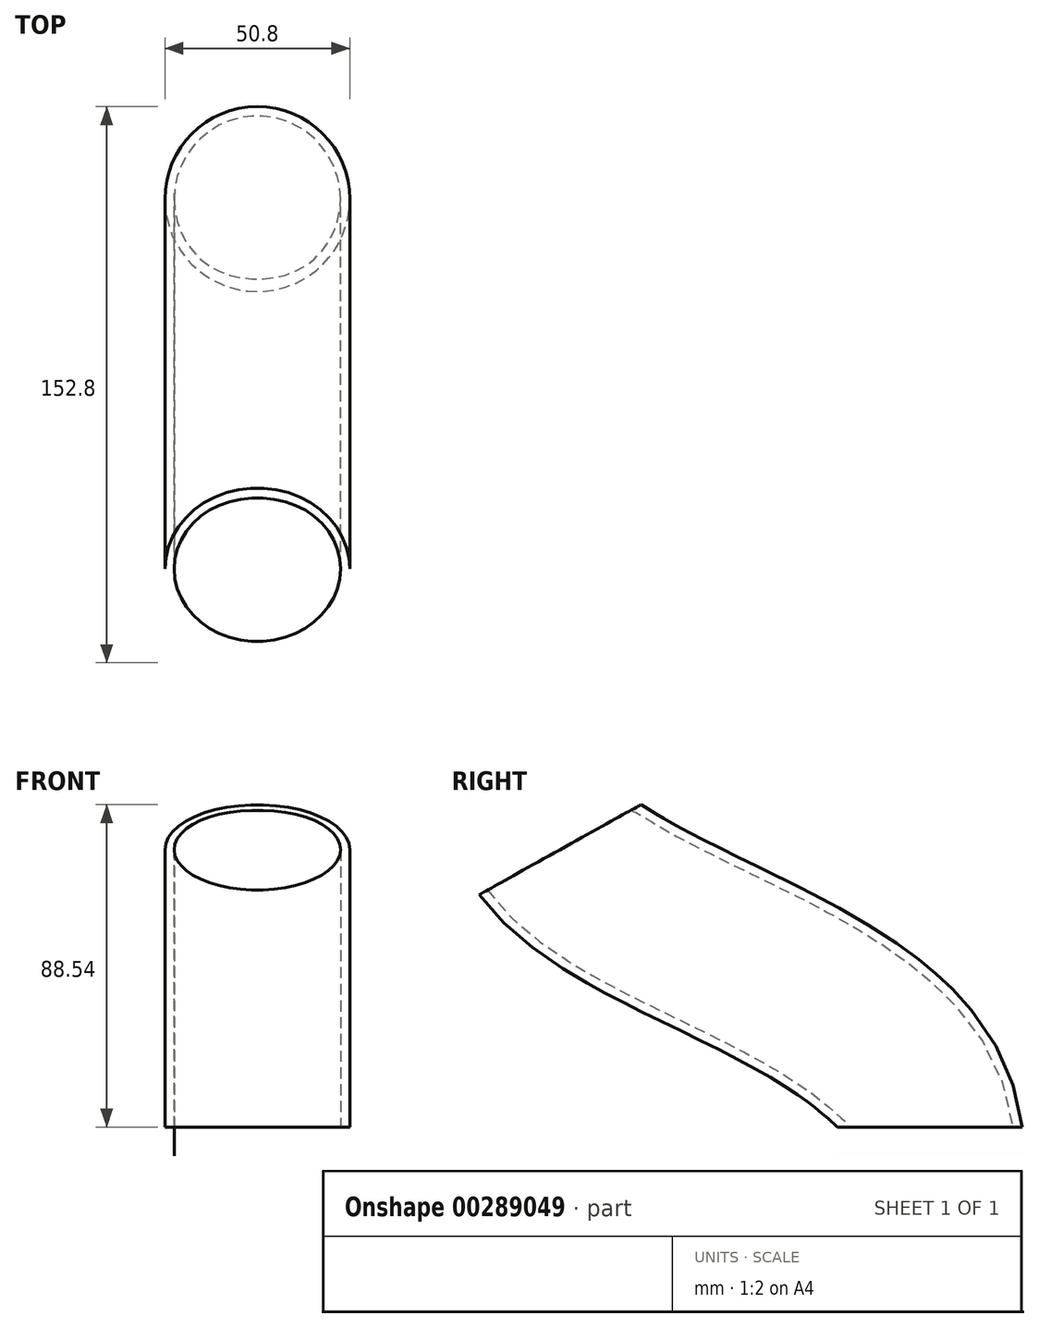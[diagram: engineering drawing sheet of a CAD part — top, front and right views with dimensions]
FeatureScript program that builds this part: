
annotation { "Feature Type Name" : "Feature", "Feature Type Description" : "" }
export const myFeature = defineFeature(function(context is Context, id is Id, definition is map)
    precondition{}
    {
        {
            var Q0;
            Q0=qCreatedBy(makeId("Top.planeOp"),FACE);
            var sketch = newSketch(context, id + "F0", { "sketchPlane" : qUnion([Q0])});
            skLineSegment(sketch, "E0", {"start": v(-86.84, 0) * mm, "end": v(86.84, 0) * mm, "construction": true});
            skLineSegment(sketch, "E1", {"start": v(0, 36.26) * mm, "end": v(0, -36.26) * mm, "construction": true});
            skCircle(sketch, "E2", {"center": v(0, 0) * mm, "radius": 25.4 * mm});
            skSolve(sketch);
        }
        {
            var Q0;
            Q0=qCreatedBy(makeId("Right.planeOp"),FACE);
            var sketch = newSketch(context, id + "F1", { "sketchPlane" : qUnion([Q0])});
            skFitSpline(sketch, "E3", {"points": [v(0, 0) * mm, v(-101.6, 76.2) * mm], "startDerivative": vector(-22.86, 114.3) * mm, "endDerivative": vector(-64.77, 76.2) * mm});
            skSolve(sketch);
        }
        {
            var Q0;
            Q0=sQuery(id+"F1.wireOp",EDGE,"E3");
            var Q1;
            Q1=sQuery(id+"F1.wireOp",VERTEX,"E3.1.internal");
            cPlane(context, id + "F2", {"entities" : qUnion([Q0, Q1]), "cplaneType" : CPlaneType.CURVE_POINT, "offset" : 25.4 * mm, "width" : 152.4 * mm, "height" : 152.4 * mm});
        }
        {
            var Q0;
            Q0=makeQuery(id+"F0.imprint","IMPRINT",FACE,{"disambiguationData":[TD([[makeQuery(id+"F0.imprint","IMPRINT",EDGE,{"derivedFrom":sQuery(id+"F0.wireOp",EDGE,"E2")}),1.0]])]});
            var Q1;
            Q1=sQuery(id+"F1.wireOp",EDGE,"E3");
            sweep(context, id + "F3", {"profiles" : qUnion([Q0]), "path" : qUnion([Q1])});
        }
        {
            var Q0;
            Q0=makeQuery(id+"F3.opSweep","CAP_FACE",FACE,{"disambiguationData":[OSD([sQuery(id+"F0.wireOp",EDGE,"E2"),sQuery(id+"F1.wireOp",VERTEX,"E3.end")])],"isStart":false});
            var Q1;
            Q1=makeQuery(id+"F3.opSweep","CAP_FACE",FACE,{"disambiguationData":[OSD([sQuery(id+"F0.wireOp",EDGE,"E2"),sQuery(id+"F1.wireOp",VERTEX,"E3.start")])],"isStart":true});
            shell(context, id + "F4", {"entities" : qUnion([Q0, Q1]), "thickness" : 2.54 * mm});
        }
    });
